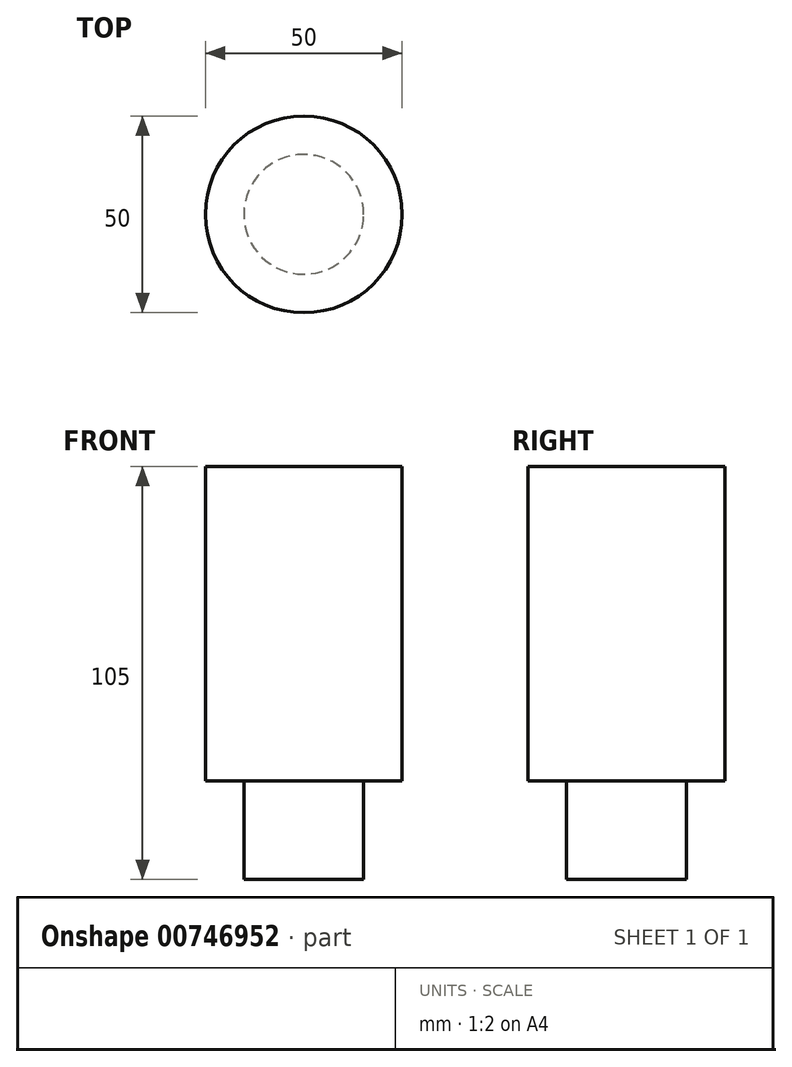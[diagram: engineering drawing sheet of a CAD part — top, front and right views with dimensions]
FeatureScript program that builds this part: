
annotation { "Feature Type Name" : "Feature", "Feature Type Description" : "" }
export const myFeature = defineFeature(function(context is Context, id is Id, definition is map)
    precondition{}
    {
        {
            var Q0;
            Q0=qCreatedBy(makeId("Top.planeOp"),FACE);
            var sketch = newSketch(context, id + "F0", { "sketchPlane" : qUnion([Q0])});
            skCircle(sketch, "E0", {"center": v(-17.94, 17.4) * mm, "radius": 25 * mm});
            skSolve(sketch);
        }
        {
            var Q0;
            Q0=makeQuery(id+"F0.imprint","IMPRINT",FACE,{"disambiguationData":[TD([[makeQuery(id+"F0.imprint","IMPRINT",EDGE,{"derivedFrom":sQuery(id+"F0.wireOp",EDGE,"E0")}),1.0]])]});
            extrude(context, id + "F1", {"entities" : qUnion([Q0]), "depth" : 80 * mm, "offsetDistance" : 25 * mm});
        }
        {
            var Q0;
            Q0=makeQuery(id+"F1.opExtrude","CAP_FACE",FACE,{"disambiguationData":[OSD([sQuery(id+"F0.wireOp",EDGE,"E0")])],"isStart":true});
            var sketch = newSketch(context, id + "F2", { "sketchPlane" : qUnion([Q0])});
            skCircle(sketch, "E1", {"center": v(-17.94, -17.4) * mm, "radius": 15.22 * mm});
            skSolve(sketch);
        }
        {
            var Q0;
            Q0=makeQuery(id+"F2.imprint","IMPRINT",FACE,{"disambiguationData":[TD([[makeQuery(id+"F2.imprint","IMPRINT",EDGE,{"derivedFrom":sQuery(id+"F2.wireOp",EDGE,"E1")}),1.0]])]});
            var sketch = newSketch(context, id + "F3", { "sketchPlane" : qUnion([Q0])});
            skSolve(sketch);
        }
        {
            var Q0;
            Q0 = qSketchRegion(id + "F3", true);
            var Q1;
            Q1=makeQuery(id+"F3.imprint","IMPRINT",FACE,{"disambiguationData":[TD([[makeQuery(id+"F3.imprint","IMPRINT",EDGE,{"derivedFrom":makeQuery(id+"F2.imprint","IMPRINT",EDGE,{"derivedFrom":sQuery(id+"F2.wireOp",EDGE,"E1")})}),1.0]])]});
            extrude(context, id + "F4", {"entities" : qUnion([Q0, Q1]), "operationType" : NewBodyOperationType.ADD, "depth" : 25 * mm, "offsetDistance" : 25 * mm});
        }
    });
